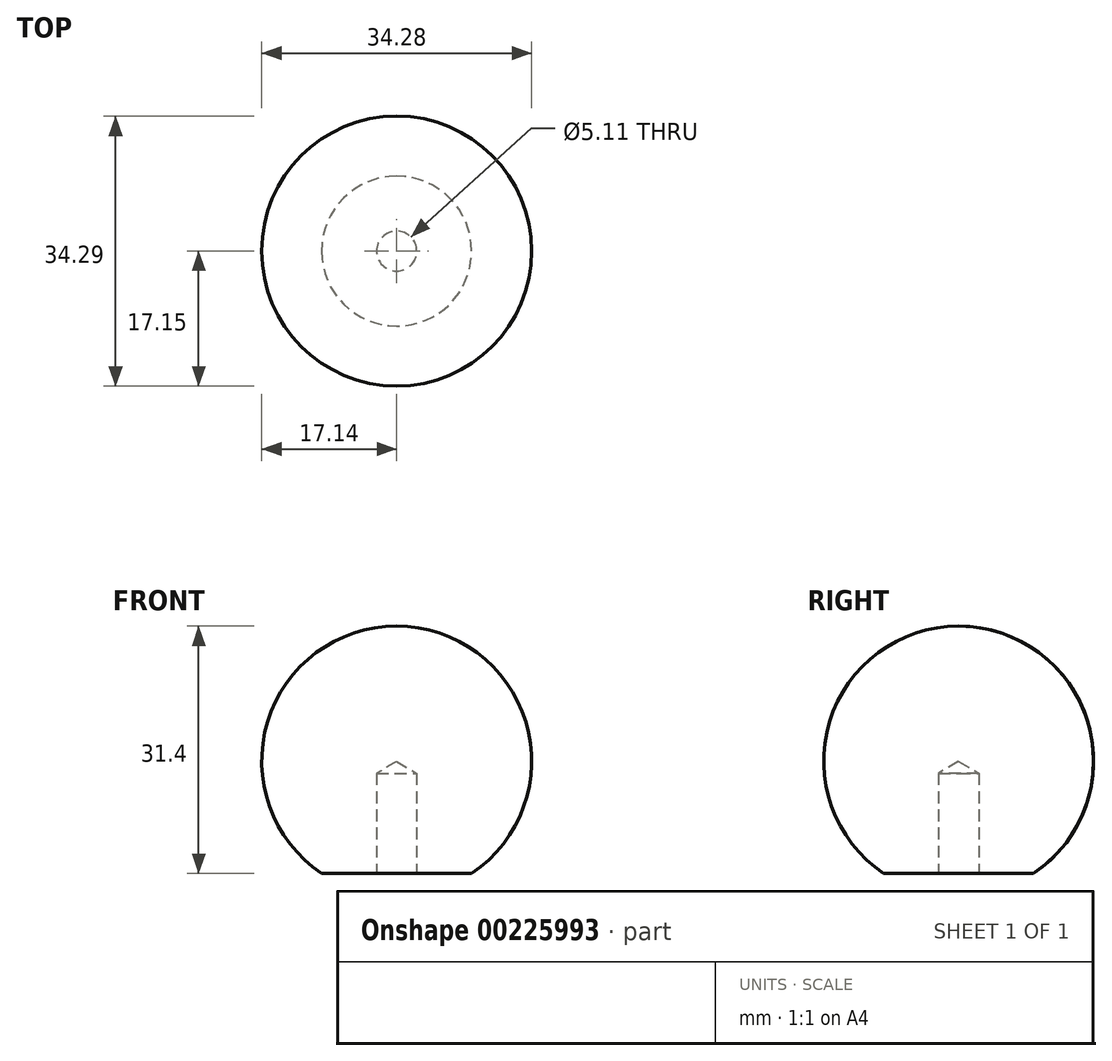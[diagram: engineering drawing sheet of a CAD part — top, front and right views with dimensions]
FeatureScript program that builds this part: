
annotation { "Feature Type Name" : "Feature", "Feature Type Description" : "" }
export const myFeature = defineFeature(function(context is Context, id is Id, definition is map)
    precondition{}
    {
        {
            var Q0;
            Q0=qCreatedBy(makeId("Right.planeOp"),FACE);
            var sketch = newSketch(context, id + "F0", { "sketchPlane" : qUnion([Q0])});
            skCircle(sketch, "E0", {"center": v(0, 0) * mm, "radius": 17.15 * mm, "construction": true});
            skArc(sketch, "E1", {"start": v(0, 17.15) * mm, "mid": v(-16.4, 4.98) * mm, "end": v(-9.53, -14.26) * mm});
            skLineSegment(sketch, "E2", {"start": v(-9.53, -14.26) * mm, "end": v(0, -14.26) * mm});
            skLineSegment(sketch, "E3", {"start": v(0, -14.26) * mm, "end": v(0, 17.14) * mm});
            skSolve(sketch);
        }
        {
            var Q0;
            Q0 = qSketchRegion(id + "F0", true);
            var Q1;
            Q1=sQuery(id+"F0.wireOp",EDGE,"E3");
            revolve(context, id + "F1", {"entities" : qUnion([Q0]), "axis" : qUnion([Q1]), "revolveType" : RevolveType.FULL});
        }
        {
            var Q0;
            Q0=makeQuery(id+"F1.opRevolve","SWEPT_FACE",FACE,{"disambiguationData":[OSD([sQuery(id+"F0.wireOp",EDGE,"E2")])]});
            var sketch = newSketch(context, id + "F2", { "sketchPlane" : qUnion([Q0])});
            skPoint(sketch, "E4", {"position": v(0, 0) * mm});
            skSolve(sketch);
        }
        {
            var Q0;
            Q0=sQuery(id+"F2.wireOp",VERTEX,"E4");
            var Q1;
            Q1=makeQuery(id+"F1.opRevolve","SWEPT_BODY",BODY,{"disambiguationData":[OSD([sQuery(id+"F0.wireOp",EDGE,"E1"),sQuery(id+"F0.wireOp",EDGE,"E2"),sQuery(id+"F0.wireOp",EDGE,"E3")])]});
            hole(context, id + "F3", {"style" : HoleStyle.SIMPLE, "endStyle" : HoleEndStyle.BLIND, "standardTappedOrClearance" : lookupTablePath({ "standard" : "ANSI", "engagement" : "75%", "pitch" : "20 tpi", "size" : "1/4", "type" : "Tapped" }), "standardBlindInLast" : lookupTablePath({ "standard" : "ANSI", "engagement" : "75%", "pitch" : "20 tpi", "size" : "1/4", "type" : "Tapped" }), "holeDiameter" : 5.1 * mm, "holeDepth" : 12.7 * mm, "locations" : qUnion([Q0]), "scope" : qUnion([Q1]), "majorDiameter" : 6.35 * mm});
        }
    });
